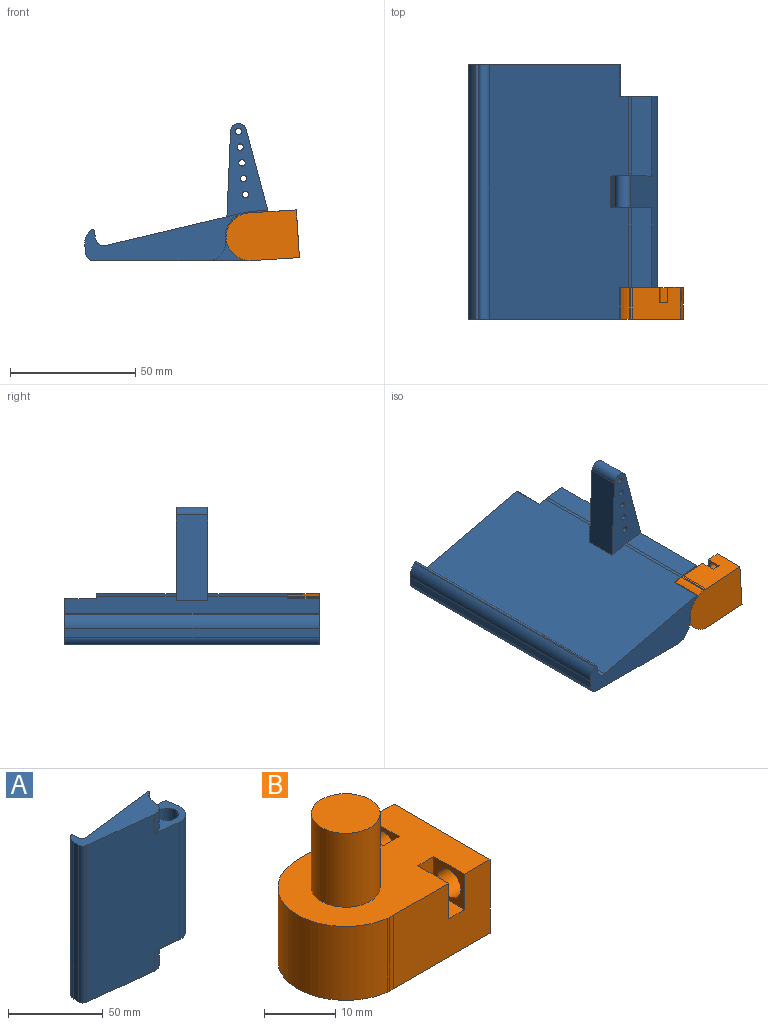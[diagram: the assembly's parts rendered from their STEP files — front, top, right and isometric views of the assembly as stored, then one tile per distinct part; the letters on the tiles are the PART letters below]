
ASSEMBLY  parts=2 mates=1
PART A: 35 faces, bbox 75.4x55x101.6 mm
  f0: plane 76.2x41.38mm, normal (0.99,0.15,0), area 1076mm2, adj f2,f8,f21,f24,f25,f27,f29,f30
  f1: plane 33.86x12.7mm, normal (-0.99,0.15,0), area 434.9mm2, adj f2,f12,f27,f30
  f2: cylinder r=3.17mm len=12.7mm, axis (0,0,-1), area 114.5mm2, adj f0,f1,f27,f30
  f3: cylinder r=1.27mm len=12.7mm, axis (0,0,-1), area 101.3mm2, adj f27,f30
  f4: cylinder r=1.27mm len=12.7mm, axis (0,0,-1), area 101.3mm2, adj f27,f30
  f5: cylinder r=1.27mm len=12.7mm, axis (0,0,-1), area 101.3mm2, adj f27,f30
  f6: cylinder r=1.27mm len=12.7mm, axis (0,0,-1), area 101.3mm2, adj f27,f30
  f7: cylinder r=1.27mm len=12.7mm, axis (0,0,-1), area 101.3mm2, adj f27,f30
  f8: cylinder r=9.53mm len=76.2mm, axis (0,0,-1), area 1315.1mm2, adj f0,f9,f21,f24
  f9: plane 101.6x62.19mm, normal (-0.11,-0.99,0), area 5927.1mm2, adj f8,f11,f19,f20,f21,f24,f31,f32
  f10: cylinder r=5.71mm len=76.2mm, axis (0,0,-1), area 2736.2mm2, adj f21,f24
  f11: plane 61.49x17.5mm, normal (0,0,1), area 631.2mm2, adj f9,f12,f13,f14,f15,f16,f17,f18
  f12: plane 101.6x56.51mm, normal (-0.12,0.99,0), area 5605.6mm2, adj f1,f11,f13,f20,f21,f24,f26,f27
  f13: cylinder r=3.17mm len=101.6mm, axis (0,0,-1), area 530.1mm2, adj f11,f12,f14,f20
  f14: plane 101.6x3.37mm, normal (1,0.05,0), area 342.7mm2, adj f11,f13,f15,f20
  f15: cylinder r=0.69mm len=101.6mm, axis (0,0,-1), area 143.9mm2, adj f11,f14,f16,f20
  f16: plane 101.6x0.27mm, normal (-0.51,0.86,0), area 31.7mm2, adj f11,f15,f17,f20
  f17: cylinder r=6.35mm len=101.6mm, axis (0,0,-1), area 666.3mm2, adj f11,f16,f18,f20
  f18: plane 101.6x3.63mm, normal (-1,0,0), area 368.5mm2, adj f11,f17,f19,f20
  f19: cylinder r=3.17mm len=101.6mm, axis (0,0,-1), area 471.6mm2, adj f9,f11,f18,f20
  f20: plane 61.49x17.5mm, normal (0,0,-1), area 631.2mm2, adj f9,f12,f13,f14,f15,f16,f17,f18
  f21: plane 27.16x19.43mm, normal (0,0,-1), area 237.1mm2, adj f0,f8,f9,f10,f12,f22,f28,f29
  f22: cylinder r=9.91mm len=12.7mm, axis (0,0,-1), area 142.7mm2, adj f20,f21,f32,f33
  f23: cylinder r=9.91mm len=12.7mm, axis (0,0,-1), area 142.7mm2, adj f11,f24,f31,f34
  f24: plane 27.16x19.43mm, normal (0,0,1), area 237.1mm2, adj f0,f8,f9,f10,f12,f23,f25,f26
  f25: plane 31.75x8.13mm, normal (0,1,0), area 258.2mm2, adj f0,f24,f26,f27
  f26: cylinder r=9.91mm len=31.75mm, axis (0,0,-1), area 38.9mm2, adj f12,f24,f25,f27
  f27: plane 36.56x16.41mm, normal (0,0,1), area 361.9mm2, adj f0,f1,f2,f3,f4,f5,f6,f7
  f28: cylinder r=9.91mm len=31.75mm, axis (0,0,-1), area 38.9mm2, adj f12,f21,f29,f30
  f29: plane 31.75x8.13mm, normal (0,1,0), area 258.2mm2, adj f0,f21,f28,f30
  f30: plane 36.56x16.41mm, normal (0,0,-1), area 361.9mm2, adj f0,f1,f2,f3,f4,f5,f6,f7
  f31: cylinder r=6.99mm len=12.7mm, axis (0,0,-1), area 152.7mm2, adj f9,f11,f23,f24
  f32: cylinder r=6.99mm len=12.7mm, axis (0,0,-1), area 152.7mm2, adj f9,f20,f21,f22
  f33: cylinder r=0.32mm len=12.7mm, axis (0,0,-1), area 11.2mm2, adj f12,f20,f21,f22
  f34: cylinder r=0.32mm len=12.7mm, axis (0,0,-1), area 11.2mm2, adj f11,f12,f23,f24
PART B: 20 faces, bbox 28.7x19.1x25.4 mm
  f0: plane 19.13x12.7mm, normal (0,1,0), area 223.6mm2, adj f1,f3,f4,f7,f10,f12,f13
  f1: plane 28.66x19.05mm, normal (0,0,1), area 395.1mm2, adj f0,f2,f3,f4,f5,f6,f8,f10
  f2: plane 19.13x12.7mm, normal (0,-1,0), area 223.6mm2, adj f1,f3,f6,f7,f14,f16,f17
  f3: plane 19.05x12.7mm, normal (1,0,0), area 209.1mm2, adj f0,f1,f2,f7,f18,f19
  f4: cylinder r=9.53mm len=18.97mm, axis (0,0,-1), area 364.6mm2, adj f0,f1,f5,f7
  f5: plane 12.7x0.35mm, normal (-0.11,-0.99,0), area 4.5mm2, adj f1,f4,f6,f7
  f6: cylinder r=9.53mm len=12.7mm, axis (0,0,-1), area 10.9mm2, adj f1,f2,f5,f7
  f7: plane 28.66x19.05mm, normal (0,0,-1), area 506.9mm2, adj f0,f2,f3,f4,f5,f6
  f8: cylinder r=4.83mm len=12.7mm, axis (0,0,-1), area 385.1mm2, adj f1,f9
  f9: plane 9.65x9.65mm, normal (0,0,1), area 73.2mm2, adj f8
  f10: plane 6.1x6.1mm, normal (1,0,0), area 37.2mm2, adj f0,f1,f11,f13
  f11: plane 6.1x3.18mm, normal (0,1,0), area 19.4mm2, adj f1,f10,f12,f13
  f12: plane 6.1x6.1mm, normal (-1,0,0), area 20.7mm2, adj f0,f1,f11,f13,f19
  f13: plane 6.1x3.18mm, normal (0,0,1), area 19.4mm2, adj f0,f10,f11,f12
  f14: plane 6.1x6.1mm, normal (-1,0,0), area 20.7mm2, adj f1,f2,f15,f17,f18
  f15: plane 6.1x3.18mm, normal (0,-1,0), area 19.4mm2, adj f1,f14,f16,f17
  f16: plane 6.1x6.1mm, normal (1,0,0), area 37.2mm2, adj f1,f2,f15,f17
  f17: plane 6.1x3.18mm, normal (0,0,1), area 19.4mm2, adj f2,f14,f15,f16
  f18: cylinder r=2.29mm len=5.08mm, axis (1,0,0), area 73mm2, adj f3,f14
  f19: cylinder r=2.29mm len=5.08mm, axis (1,0,0), area 73mm2, adj f3,f12
PLACE A rot(axis=(1,-0.05,0.05),90.2deg) t=(32.75,50.8,9.52)mm fixed
PLACE B rot(axis=(-1,-0.03,-0.03),90.1deg) t=(32.75,-50.8,9.52)mm
MATE revolute A.f10 <-> B.f8  axis (0,-1,0) through (32.75,-38.1,9.52)mm
